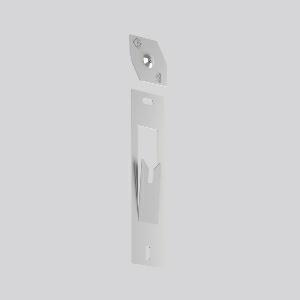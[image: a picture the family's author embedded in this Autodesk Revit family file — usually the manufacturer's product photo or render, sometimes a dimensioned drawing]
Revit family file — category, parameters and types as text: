
# Revit family: linedo_wand_adapter_982814_000_9ddb
name_source: partatom
category: Lighting Fixtures
units: mm (PartAtom-declared; Revit-internal decimal feet)

## family parameters
Cut with Voids When Loaded = No
Host = Face
Light Source = No
Part Type = Normal
Room Calculation Point = No
Round Connector Dimension = Use Diameter
Shared = No

## types (1)
- LINEDO Wand Adapter
    Apparent Load = 0 VA
    Default Elevation = 1800 mm
    Description = Wall mounting made of galvanised sheet steel. For vertical installation of LINEDO luminaire modules. 2 wall suspensions are required per luminaire module (max. 1 x 8 units). With this accessory, the protection type of the luminaire module can be reduced to IP 20.
Colour: unpainted
Length: 200 mm
Width: 53 mm
Height: 9 mm
Weight: 121 g
Type of Installation: Wall (surface)
    Height = 9 mm  [stored 0.0295276 ft]
    Lamp = 0 x
    Length = 200 mm  [stored 0.656168 ft]
    Luminous efficacy = 0 lm/W
    Manufacturer = RZB
    ModVariant = No
    Model = 982814.000
    Mounting Place = Ceiling
    Mounting Type = Surface mounted
    Number of Poles = 1
    OnlyDefault = Yes
    Power Factor = 1
    Product Name = LINEDO Wand Adapter
    Product group = Continuous line luminaire system Linedo IP 54
    ProductGroupID = 314
    Protection Class = Protection class
    Protection Degree = Degree of protection
    RLX_Detail_Level = 1
    RLX_Emergency_Light_Flux = 0 lm
    RLX_Emergency_Type = 0
    RLX_Emergency_Type_DB = No
    RlxData = <blob elided: 10245 chars, md5=d7004a52>
    Standby Power = 0 W
    System Light Flux = 0 lm
    System Power = 0 W
    Type Comments = Product without accessories
    Type Image = 982814.000.jpg
    URL = http://relux.com
    VarID = ---
    Voltage = 0 V
    Weight = 0.00 kg
    Width = 53 mm

note: [stored X ft] marks values corroborated as IEEE doubles in the binary element streams (Revit-internal decimal feet)

## geometry (parser evidence)
native form markers: Sweep x10
no freeform markers — native parametric forms only
